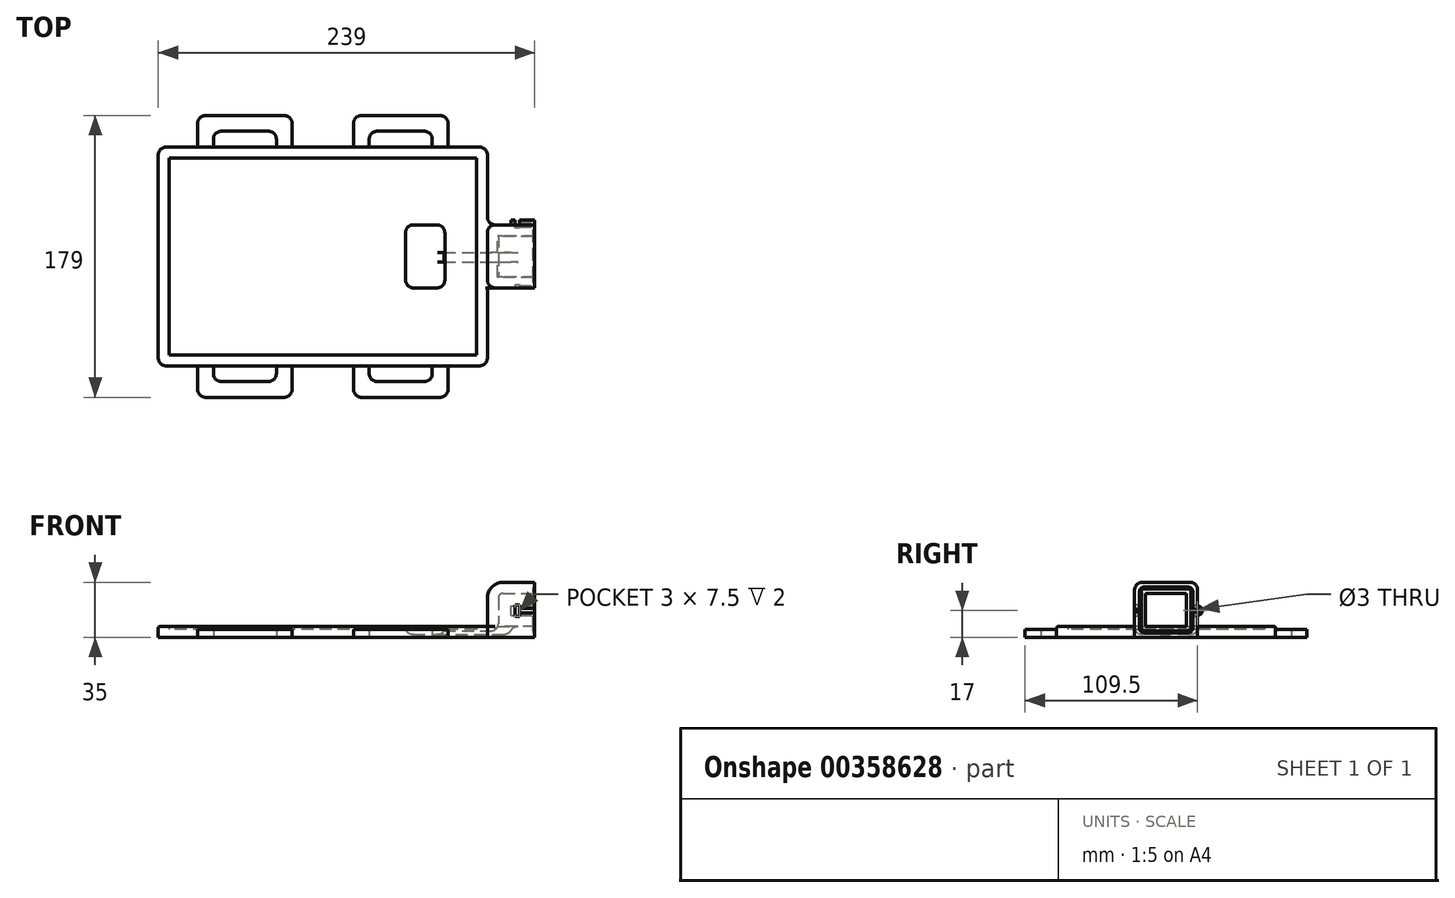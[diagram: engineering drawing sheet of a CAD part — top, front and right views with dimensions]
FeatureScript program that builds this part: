
annotation { "Feature Type Name" : "Feature", "Feature Type Description" : "" }
export const myFeature = defineFeature(function(context is Context, id is Id, definition is map)
    precondition{}
    {
        {
            var Q0;
            Q0=qCreatedBy(makeId("Top.planeOp"),FACE);
            var sketch = newSketch(context, id + "F0", { "sketchPlane" : qUnion([Q0])});
            skLineSegment(sketch, "E0.bottom", {"start": v(0, 0) * mm, "end": v(195, 0) * mm});
            skLineSegment(sketch, "E0.top", {"start": v(0, 125) * mm, "end": v(195, 125) * mm});
            skLineSegment(sketch, "E0.left", {"start": v(0, 0) * mm, "end": v(0, 125) * mm});
            skLineSegment(sketch, "E0.right", {"start": v(195, 0) * mm, "end": v(195, 125) * mm});
            skLineSegment(sketch, "E1.0", {"start": v(-7, 132) * mm, "end": v(202, 132) * mm});
            skLineSegment(sketch, "E1.1", {"start": v(-7, -7) * mm, "end": v(-7, 132) * mm});
            skLineSegment(sketch, "E1.2", {"start": v(-7, -7) * mm, "end": v(202, -7) * mm});
            skLineSegment(sketch, "E1.3", {"start": v(202, -7) * mm, "end": v(202, 132) * mm});
            skSolve(sketch);
        }
        {
            var Q0;
            Q0=makeQuery(id+"F0.imprint","IMPRINT",FACE,{"disambiguationData":[TD([[makeQuery(id+"F0.imprint","IMPRINT",EDGE,{"derivedFrom":sQuery(id+"F0.wireOp",EDGE,"E0.bottom")}),-1.0]])]});
            var Q1;
            Q1=makeQuery(id+"F0.imprint","IMPRINT",FACE,{"disambiguationData":[TD([[makeQuery(id+"F0.imprint","IMPRINT",EDGE,{"derivedFrom":sQuery(id+"F0.wireOp",EDGE,"E0.bottom")}),1.0]])]});
            extrude(context, id + "F1", {"entities" : qUnion([Q0, Q1]), "depth" : 5 * mm});
        }
        {
            var Q0;
            Q0 = qSketchRegion(id + "F0", true);
            extrude(context, id + "F2", {"entities" : qUnion([Q0]), "operationType" : NewBodyOperationType.ADD, "depth" : 7 * mm});
        }
        {
            var Q0;
            Q0=makeQuery(id+"F1.opExtrude","CAP_FACE",FACE,{"disambiguationData":[OSD([sQuery(id+"F0.wireOp",EDGE,"E1.0"),sQuery(id+"F0.wireOp",EDGE,"E1.1"),sQuery(id+"F0.wireOp",EDGE,"E1.2"),sQuery(id+"F0.wireOp",EDGE,"E1.3")])],"isStart":false});
            var sketch = newSketch(context, id + "F3", { "sketchPlane" : qUnion([Q0])});
            skLineSegment(sketch, "E2.bottom", {"start": v(150, 82.5) * mm, "end": v(175, 82.5) * mm});
            skLineSegment(sketch, "E2.top", {"start": v(150, 42.5) * mm, "end": v(175, 42.5) * mm});
            skLineSegment(sketch, "E2.left", {"start": v(150, 82.5) * mm, "end": v(150, 42.5) * mm});
            skLineSegment(sketch, "E2.right", {"start": v(175, 82.5) * mm, "end": v(175, 42.5) * mm});
            skSolve(sketch);
        }
        {
            var Q0;
            Q0=makeQuery(id+"F3.imprint","IMPRINT",FACE,{"disambiguationData":[TD([[makeQuery(id+"F3.imprint","IMPRINT",EDGE,{"derivedFrom":sQuery(id+"F3.wireOp",EDGE,"E2.bottom")}),-1.0]])]});
            extrude(context, id + "F4", {"entities" : qUnion([Q0]), "operationType" : NewBodyOperationType.REMOVE, "oppositeDirection" : true, "depth" : 3 * mm});
        }
        {
            var Q0;
            Q0=makeQuery(id+"F4.boolean.opBoolean","COPY",EDGE,{"derivedFrom":makeQuery(id+"F4.opExtrude","SWEPT_EDGE",EDGE,{"disambiguationData":[OSD([sQuery(id+"F3.wireOp",EDGE,"E2.bottom"),sQuery(id+"F3.wireOp",EDGE,"E2.left")])]})});
            var Q1;
            Q1=makeQuery(id+"F4.boolean.opBoolean","COPY",EDGE,{"derivedFrom":makeQuery(id+"F4.opExtrude","SWEPT_EDGE",EDGE,{"disambiguationData":[OSD([sQuery(id+"F3.wireOp",EDGE,"E2.bottom"),sQuery(id+"F3.wireOp",EDGE,"E2.right")])]})});
            var Q2;
            Q2=makeQuery(id+"F4.boolean.opBoolean","COPY",EDGE,{"derivedFrom":makeQuery(id+"F4.opExtrude","SWEPT_EDGE",EDGE,{"disambiguationData":[OSD([sQuery(id+"F3.wireOp",EDGE,"E2.top"),sQuery(id+"F3.wireOp",EDGE,"E2.right")])]})});
            var Q3;
            Q3=makeQuery(id+"F4.boolean.opBoolean","COPY",EDGE,{"derivedFrom":makeQuery(id+"F4.opExtrude","SWEPT_EDGE",EDGE,{"disambiguationData":[OSD([sQuery(id+"F3.wireOp",EDGE,"E2.top"),sQuery(id+"F3.wireOp",EDGE,"E2.left")])]})});
            fillet(context, id + "F5", {"entities" : qUnion([Q0, Q1, Q2, Q3]), "radius" : 5 * mm, "tangentPropagation" : true, "allowEdgeOverflow" : false});
        }
        {
            var Q0;
            Q0=makeQuery(id+"F4.boolean.opBoolean","COPY",FACE,{"derivedFrom":makeQuery(id+"F4.opExtrude","CAP_FACE",FACE,{"disambiguationData":[OSD([sQuery(id+"F3.wireOp",EDGE,"E2.bottom"),sQuery(id+"F3.wireOp",EDGE,"E2.top"),sQuery(id+"F3.wireOp",EDGE,"E2.left"),sQuery(id+"F3.wireOp",EDGE,"E2.right")])],"isStart":false})});
            fillet(context, id + "F6", {"entities" : qUnion([Q0]), "radius" : 5 * mm, "tangentPropagation" : true, "allowEdgeOverflow" : false});
        }
        {
            var Q0;
            {var subQ0=sQuery(id+"F0.wireOp",EDGE,"E1.3");Q0=makeQuery(id+"F2.boolean.opBoolean","MERGE",FACE,{"derivedFrom":[makeQuery(id+"F1.opExtrude","SWEPT_FACE",FACE,{"disambiguationData":[OSD([subQ0])]}),makeQuery(id+"F2.opExtrude","SWEPT_FACE",FACE,{"disambiguationData":[OSD([subQ0])]})]});}
            var sketch = newSketch(context, id + "F7", { "sketchPlane" : qUnion([Q0])});
            skLineSegment(sketch, "E3.bottom", {"start": v(42.5, 0) * mm, "end": v(82.5, 0) * mm});
            skLineSegment(sketch, "E3.top", {"start": v(42.5, 35) * mm, "end": v(82.5, 35) * mm});
            skLineSegment(sketch, "E3.left", {"start": v(42.5, 0) * mm, "end": v(42.5, 35) * mm});
            skLineSegment(sketch, "E3.right", {"start": v(82.5, 0) * mm, "end": v(82.5, 35) * mm});
            skSolve(sketch);
        }
        {
            var Q0;
            {var subQ0=sQuery(id+"F7.wireOp",EDGE,"E3.top");Q0=makeQuery(id+"F7.imprint","IMPRINT",FACE,{"disambiguationData":[TD([[makeQuery(id+"F7.imprint","IMPRINT",EDGE,{"derivedFrom":subQ0}),-1.0]])]});}
            var Q1;
            {var subQ0=sQuery(id+"F7.wireOp",EDGE,"E3.bottom");Q1=makeQuery(id+"F7.imprint","IMPRINT",FACE,{"disambiguationData":[TD([[makeQuery(id+"F7.imprint","IMPRINT",EDGE,{"derivedFrom":subQ0}),1.0]])]});}
            extrude(context, id + "F8", {"entities" : qUnion([Q0, Q1]), "operationType" : NewBodyOperationType.ADD, "depth" : 30 * mm});
        }
        {
            var Q0;
            Q0=makeQuery(id+"F8.opExtrude","CAP_EDGE",EDGE,{"disambiguationData":[OSD([sQuery(id+"F7.wireOp",EDGE,"E3.top")])],"isStart":true});
            fillet(context, id + "F9", {"entities" : qUnion([Q0]), "radius" : 10 * mm, "tangentPropagation" : true, "allowEdgeOverflow" : false});
        }
        {
            var Q0;
            Q0=makeQuery(id+"F8.opExtrude","SWEPT_EDGE",EDGE,{"disambiguationData":[OSD([sQuery(id+"F7.wireOp",EDGE,"E3.top"),sQuery(id+"F7.wireOp",EDGE,"E3.left")])]});
            var Q1;
            Q1=makeQuery(id+"F8.opExtrude","SWEPT_EDGE",EDGE,{"disambiguationData":[OSD([sQuery(id+"F7.wireOp",EDGE,"E3.top"),sQuery(id+"F7.wireOp",EDGE,"E3.right")])]});
            fillet(context, id + "F10", {"entities" : qUnion([Q0, Q1]), "radius" : 5 * mm, "tangentPropagation" : true, "allowEdgeOverflow" : false});
        }
        {
            var Q0;
            {var subQ0=sQuery(id+"F0.wireOp",EDGE,"E1.3");var subQ1=sQuery(id+"F7.wireOp",EDGE,"E3.left");Q0=makeQuery(id+"F8.boolean.opBoolean","SPLIT",EDGE,{"disambiguationData":[topologyDisambiguationEdgeConnected([makeQuery(id+"F1.opExtrude","SWEPT_FACE",FACE,{"disambiguationData":[OSD([subQ0])]})])],"derivedFrom":makeQuery(id+"F8.opExtrude","CAP_EDGE",EDGE,{"disambiguationData":[OSD([subQ1])],"isStart":true})});}
            var Q1;
            {var subQ0=sQuery(id+"F0.wireOp",EDGE,"E1.3");var subQ1=sQuery(id+"F7.wireOp",EDGE,"E3.right");Q1=makeQuery(id+"F8.boolean.opBoolean","SPLIT",EDGE,{"disambiguationData":[topologyDisambiguationEdgeConnected([makeQuery(id+"F1.opExtrude","SWEPT_FACE",FACE,{"disambiguationData":[OSD([subQ0])]})])],"derivedFrom":makeQuery(id+"F8.opExtrude","CAP_EDGE",EDGE,{"disambiguationData":[OSD([subQ1])],"isStart":true})});}
            fillet(context, id + "F11", {"entities" : qUnion([Q0, Q1]), "radius" : 5 * mm, "tangentPropagation" : true, "allowEdgeOverflow" : false});
        }
        {
            var Q0;
            Q0=makeQuery(id+"F8.opExtrude","CAP_FACE",FACE,{"disambiguationData":[OSD([sQuery(id+"F7.wireOp",EDGE,"E3.bottom"),sQuery(id+"F7.wireOp",EDGE,"E3.top"),sQuery(id+"F7.wireOp",EDGE,"E3.left"),sQuery(id+"F7.wireOp",EDGE,"E3.right")])],"isStart":false});
            shell(context, id + "F12", {"entities" : qUnion([Q0]), "thickness" : 7 * mm});
        }
        {
            var Q0;
            Q0=makeQuery(id+"F8.opExtrude","CAP_FACE",FACE,{"disambiguationData":[OSD([sQuery(id+"F7.wireOp",EDGE,"E3.bottom"),sQuery(id+"F7.wireOp",EDGE,"E3.top"),sQuery(id+"F7.wireOp",EDGE,"E3.left"),sQuery(id+"F7.wireOp",EDGE,"E3.right")])],"isStart":false});
            var sketch = newSketch(context, id + "F13", { "sketchPlane" : qUnion([Q0])});
            skPoint(sketch, "E4.0", {"position": v(43.96, 33.54) * mm});
            skPoint(sketch, "E5.0", {"position": v(81.04, 33.54) * mm});
            skLineSegment(sketch, "E6.0", {"start": v(48.5, 32) * mm, "end": v(76.5, 32) * mm});
            skLineSegment(sketch, "E6.1", {"start": v(45.5, 6) * mm, "end": v(45.5, 29) * mm});
            skLineSegment(sketch, "E6.2", {"start": v(48.5, 3) * mm, "end": v(76.5, 3) * mm});
            skLineSegment(sketch, "E6.3", {"start": v(79.5, 6) * mm, "end": v(79.5, 29) * mm});
            skPoint(sketch, "E7.visualSharp", {"position": v(45.5, 32) * mm});
            skArc(sketch, "E7.filletArc", {"start": v(48.5, 32) * mm, "mid": v(46.38, 31.12) * mm, "end": v(45.5, 29) * mm});
            skPoint(sketch, "E8.visualSharp", {"position": v(79.5, 32) * mm});
            skArc(sketch, "E8.filletArc", {"start": v(79.5, 29) * mm, "mid": v(78.62, 31.12) * mm, "end": v(76.5, 32) * mm});
            skPoint(sketch, "E9.visualSharp", {"position": v(45.5, 3) * mm});
            skArc(sketch, "E9.filletArc", {"start": v(45.5, 6) * mm, "mid": v(46.38, 3.88) * mm, "end": v(48.5, 3) * mm});
            skPoint(sketch, "E10.visualSharp", {"position": v(79.5, 3) * mm});
            skArc(sketch, "E10.filletArc", {"start": v(76.5, 3) * mm, "mid": v(78.62, 3.88) * mm, "end": v(79.5, 6) * mm});
            skLineSegment(sketch, "E11.0", {"start": v(48.7, 30.8) * mm, "end": v(76.3, 30.8) * mm});
            skLineSegment(sketch, "E11.1", {"start": v(46.7, 6.2) * mm, "end": v(46.7, 28.8) * mm});
            skLineSegment(sketch, "E11.2", {"start": v(48.7, 4.2) * mm, "end": v(76.3, 4.2) * mm});
            skLineSegment(sketch, "E11.3", {"start": v(78.3, 6.2) * mm, "end": v(78.3, 28.8) * mm});
            skPoint(sketch, "E12.visualSharp", {"position": v(46.7, 30.8) * mm});
            skArc(sketch, "E12.filletArc", {"start": v(48.7, 30.8) * mm, "mid": v(47.29, 30.21) * mm, "end": v(46.7, 28.8) * mm});
            skPoint(sketch, "E13.visualSharp", {"position": v(78.3, 30.8) * mm});
            skArc(sketch, "E13.filletArc", {"start": v(78.3, 28.8) * mm, "mid": v(77.71, 30.21) * mm, "end": v(76.3, 30.8) * mm});
            skPoint(sketch, "E14.visualSharp", {"position": v(78.3, 4.2) * mm});
            skArc(sketch, "E14.filletArc", {"start": v(76.3, 4.2) * mm, "mid": v(77.71, 4.79) * mm, "end": v(78.3, 6.2) * mm});
            skPoint(sketch, "E15.visualSharp", {"position": v(46.7, 4.2) * mm});
            skArc(sketch, "E15.filletArc", {"start": v(46.7, 6.2) * mm, "mid": v(47.29, 4.79) * mm, "end": v(48.7, 4.2) * mm});
            skPoint(sketch, "E16.0.end.orphan", {"position": v(42.5, 30) * mm});
            skPoint(sketch, "E16.0.start.orphan", {"position": v(42.5, 0) * mm});
            skPoint(sketch, "E17.0.start.orphan", {"position": v(47.5, 35) * mm});
            skPoint(sketch, "E18.0.end.orphan", {"position": v(77.5, 35) * mm});
            skPoint(sketch, "E19.0.end.orphan", {"position": v(82.5, 30) * mm});
            skPoint(sketch, "E19.0.start.orphan", {"position": v(82.5, 0) * mm});
            skSolve(sketch);
        }
        {
            var Q0;
            Q0=makeQuery(id+"F13.imprint","IMPRINT",FACE,{"disambiguationData":[TD([[makeQuery(id+"F13.imprint","IMPRINT",EDGE,{"derivedFrom":sQuery(id+"F13.wireOp",EDGE,"E6.0")}),-1.0]])]});
            extrude(context, id + "F14", {"entities" : qUnion([Q0]), "operationType" : NewBodyOperationType.REMOVE, "oppositeDirection" : true, "depth" : 1 * mm});
        }
        {
            var Q0;
            {var subQ0=sQuery(id+"F7.wireOp",EDGE,"E3.right");var subQ1=sQuery(id+"F7.wireOp",EDGE,"E3.left");var subQ2=sQuery(id+"F7.wireOp",EDGE,"E3.top");var subQ3=sQuery(id+"F7.wireOp",EDGE,"E3.bottom");Q0=makeQuery(id+"F14.boolean.opBoolean","SPLIT",FACE,{"disambiguationData":[TD([makeQuery(id+"F8.opExtrude","SWEPT_FACE",FACE,{"disambiguationData":[OSD([subQ3])]})])],"derivedFrom":makeQuery(id+"F8.opExtrude","CAP_FACE",FACE,{"disambiguationData":[OSD([subQ3,subQ2,subQ1,subQ0])],"isStart":false})});}
            var sketch = newSketch(context, id + "F15", { "sketchPlane" : qUnion([Q0])});
            skCircle(sketch, "E20", {"center": v(42.5, 17) * mm, "radius": 3 * mm});
            skCircle(sketch, "E21", {"center": v(42.5, 17) * mm, "radius": 1.5 * mm});
            skCircle(sketch, "E22", {"center": v(82.5, 17) * mm, "radius": 1.5 * mm});
            skCircle(sketch, "E23", {"center": v(82.5, 17) * mm, "radius": 3 * mm});
            skSolve(sketch);
        }
        {
            var Q0;
            {var subQ0=sQuery(id+"F15.wireOp",EDGE,"E20");var subQ1=makeQuery(id+"F8.opExtrude","CAP_EDGE",EDGE,{"disambiguationData":[OSD([sQuery(id+"F7.wireOp",EDGE,"E3.left")])],"isStart":false});var subQ2=makeQuery(id+"F15.imprint","INTERSECT",VERTEX,{"disambiguationData":[OD(0.0)],"derivedFrom":[subQ1,subQ0]});Q0=makeQuery(id+"F15.imprint","IMPRINT",FACE,{"disambiguationData":[TD([[makeQuery(id+"F15.imprint","IMPRINT",EDGE,{"disambiguationData":[TD([[subQ2,-1.0]])],"derivedFrom":subQ0}),1.0]])]});}
            var Q1;
            {var subQ0=sQuery(id+"F15.wireOp",EDGE,"E22");var subQ1=makeQuery(id+"F8.opExtrude","CAP_EDGE",EDGE,{"disambiguationData":[OSD([sQuery(id+"F7.wireOp",EDGE,"E3.right")])],"isStart":false});var subQ2=makeQuery(id+"F15.imprint","INTERSECT",VERTEX,{"disambiguationData":[OD(0.0)],"derivedFrom":[subQ1,subQ0]});Q1=makeQuery(id+"F15.imprint","IMPRINT",FACE,{"disambiguationData":[TD([[makeQuery(id+"F15.imprint","IMPRINT",EDGE,{"disambiguationData":[TD([[subQ2,1.0]])],"derivedFrom":subQ0}),-1.0]])]});}
            var Q2;
            {var subQ0=sQuery(id+"F15.wireOp",EDGE,"E22");var subQ1=makeQuery(id+"F8.opExtrude","CAP_EDGE",EDGE,{"disambiguationData":[OSD([sQuery(id+"F7.wireOp",EDGE,"E3.right")])],"isStart":false});var subQ2=makeQuery(id+"F15.imprint","INTERSECT",VERTEX,{"disambiguationData":[OD(0.0)],"derivedFrom":[subQ1,subQ0]});Q2=makeQuery(id+"F15.imprint","IMPRINT",FACE,{"disambiguationData":[TD([[makeQuery(id+"F15.imprint","IMPRINT",EDGE,{"disambiguationData":[TD([[subQ2,1.0]])],"derivedFrom":subQ0}),1.0]])]});}
            var Q3;
            {var subQ0=sQuery(id+"F15.wireOp",EDGE,"E21");var subQ1=makeQuery(id+"F8.opExtrude","CAP_EDGE",EDGE,{"disambiguationData":[OSD([sQuery(id+"F7.wireOp",EDGE,"E3.left")])],"isStart":false});var subQ2=makeQuery(id+"F15.imprint","INTERSECT",VERTEX,{"disambiguationData":[OD(0.0)],"derivedFrom":[subQ1,subQ0]});Q3=makeQuery(id+"F15.imprint","IMPRINT",FACE,{"disambiguationData":[TD([[makeQuery(id+"F15.imprint","IMPRINT",EDGE,{"disambiguationData":[TD([[subQ2,-1.0]])],"derivedFrom":subQ0}),1.0]])]});}
            extrude(context, id + "F16", {"entities" : qUnion([Q0, Q1, Q2, Q3]), "operationType" : NewBodyOperationType.ADD, "oppositeDirection" : true, "depth" : 15 * mm});
        }
        {
            var Q0;
            {var subQ0=sQuery(id+"F15.wireOp",EDGE,"E22");var subQ1=makeQuery(id+"F8.opExtrude","CAP_EDGE",EDGE,{"disambiguationData":[OSD([sQuery(id+"F7.wireOp",EDGE,"E3.right")])],"isStart":false});var subQ2=makeQuery(id+"F15.imprint","INTERSECT",VERTEX,{"disambiguationData":[OD(0.0)],"derivedFrom":[subQ1,subQ0]});Q0=makeQuery(id+"F15.imprint","IMPRINT",FACE,{"disambiguationData":[TD([[makeQuery(id+"F15.imprint","IMPRINT",EDGE,{"disambiguationData":[TD([[subQ2,1.0]])],"derivedFrom":subQ0}),1.0]])]});}
            var Q1;
            {var subQ0=sQuery(id+"F15.wireOp",EDGE,"E22");var subQ1=makeQuery(id+"F8.opExtrude","CAP_EDGE",EDGE,{"disambiguationData":[OSD([sQuery(id+"F7.wireOp",EDGE,"E3.right")])],"isStart":false});var subQ2=makeQuery(id+"F15.imprint","INTERSECT",VERTEX,{"disambiguationData":[OD(0.0)],"derivedFrom":[subQ1,subQ0]});Q1=makeQuery(id+"F15.imprint","IMPRINT",FACE,{"disambiguationData":[TD([[makeQuery(id+"F15.imprint","IMPRINT",EDGE,{"disambiguationData":[TD([[subQ2,-1.0]])],"derivedFrom":subQ0}),1.0]])]});}
            var Q2;
            {var subQ0=sQuery(id+"F15.wireOp",EDGE,"E21");var subQ1=makeQuery(id+"F8.opExtrude","CAP_EDGE",EDGE,{"disambiguationData":[OSD([sQuery(id+"F7.wireOp",EDGE,"E3.left")])],"isStart":false});var subQ2=makeQuery(id+"F15.imprint","INTERSECT",VERTEX,{"disambiguationData":[OD(0.0)],"derivedFrom":[subQ1,subQ0]});Q2=makeQuery(id+"F15.imprint","IMPRINT",FACE,{"disambiguationData":[TD([[makeQuery(id+"F15.imprint","IMPRINT",EDGE,{"disambiguationData":[TD([[subQ2,-1.0]])],"derivedFrom":subQ0}),1.0]])]});}
            var Q3;
            {var subQ0=sQuery(id+"F15.wireOp",EDGE,"E21");var subQ1=makeQuery(id+"F8.opExtrude","CAP_EDGE",EDGE,{"disambiguationData":[OSD([sQuery(id+"F7.wireOp",EDGE,"E3.left")])],"isStart":false});var subQ2=makeQuery(id+"F15.imprint","INTERSECT",VERTEX,{"disambiguationData":[OD(0.0)],"derivedFrom":[subQ1,subQ0]});Q3=makeQuery(id+"F15.imprint","IMPRINT",FACE,{"disambiguationData":[TD([[makeQuery(id+"F15.imprint","IMPRINT",EDGE,{"disambiguationData":[TD([[subQ2,1.0]])],"derivedFrom":subQ0}),1.0]])]});}
            extrude(context, id + "F17", {"entities" : qUnion([Q0, Q1, Q2, Q3]), "operationType" : NewBodyOperationType.REMOVE, "oppositeDirection" : true, "depth" : 10 * mm});
        }
        {
            var Q0;
            Q0=makeQuery(id+"F8.opExtrude","SWEPT_FACE",FACE,{"disambiguationData":[OSD([sQuery(id+"F7.wireOp",EDGE,"E3.left")])]});
            var sketch = newSketch(context, id + "F18", { "sketchPlane" : qUnion([Q0])});
            skLineSegment(sketch, "E24.bottom", {"start": v(219.5, 20.7) * mm, "end": v(222.5, 20.7) * mm});
            skLineSegment(sketch, "E24.top", {"start": v(219.5, 13.2) * mm, "end": v(222.5, 13.2) * mm});
            skLineSegment(sketch, "E24.left", {"start": v(219.5, 20.7) * mm, "end": v(219.5, 13.2) * mm});
            skLineSegment(sketch, "E24.right", {"start": v(222.5, 20.7) * mm, "end": v(222.5, 13.2) * mm});
            skSolve(sketch);
        }
        {
            var Q0;
            Q0 = qSketchRegion(id + "F18", true);
            extrude(context, id + "F19", {"entities" : qUnion([Q0]), "operationType" : NewBodyOperationType.REMOVE, "oppositeDirection" : true, "depth" : 2 * mm, "hasSecondDirection" : true, "secondDirectionOppositeDirection" : false, "secondDirectionDepth" : 25 * mm});
        }
        {
            var Q0;
            Q0=makeQuery(id+"F8.opExtrude","SWEPT_FACE",FACE,{"disambiguationData":[OSD([sQuery(id+"F7.wireOp",EDGE,"E3.right")])]});
            var sketch = newSketch(context, id + "F20", { "sketchPlane" : qUnion([Q0])});
            skLineSegment(sketch, "E25.bottom", {"start": v(-222.5, 20.7) * mm, "end": v(-219.5, 20.7) * mm});
            skLineSegment(sketch, "E25.top", {"start": v(-222.5, 13.2) * mm, "end": v(-219.5, 13.2) * mm});
            skLineSegment(sketch, "E25.left", {"start": v(-222.5, 20.7) * mm, "end": v(-222.5, 13.2) * mm});
            skLineSegment(sketch, "E25.right", {"start": v(-219.5, 20.7) * mm, "end": v(-219.5, 13.2) * mm});
            skSolve(sketch);
        }
        {
            var Q0;
            Q0 = qSketchRegion(id + "F20", true);
            extrude(context, id + "F21", {"entities" : qUnion([Q0]), "operationType" : NewBodyOperationType.REMOVE, "oppositeDirection" : true, "depth" : 2 * mm, "hasSecondDirection" : true, "secondDirectionOppositeDirection" : false, "secondDirectionDepth" : 25 * mm});
        }
        {
            var Q0;
            {var subQ0=sQuery(id+"F0.wireOp",EDGE,"E1.3");var subQ1=sQuery(id+"F0.wireOp",EDGE,"E1.0");Q0=makeQuery(id+"F2.boolean.opBoolean","MERGE",EDGE,{"derivedFrom":[makeQuery(id+"F1.opExtrude","SWEPT_EDGE",EDGE,{"disambiguationData":[OSD([subQ1,subQ0])]}),makeQuery(id+"F2.opExtrude","SWEPT_EDGE",EDGE,{"disambiguationData":[OSD([subQ1,subQ0])]})]});}
            var Q1;
            {var subQ0=sQuery(id+"F0.wireOp",EDGE,"E1.3");var subQ1=sQuery(id+"F0.wireOp",EDGE,"E1.2");Q1=makeQuery(id+"F2.boolean.opBoolean","MERGE",EDGE,{"derivedFrom":[makeQuery(id+"F1.opExtrude","SWEPT_EDGE",EDGE,{"disambiguationData":[OSD([subQ1,subQ0])]}),makeQuery(id+"F2.opExtrude","SWEPT_EDGE",EDGE,{"disambiguationData":[OSD([subQ1,subQ0])]})]});}
            var Q2;
            {var subQ0=sQuery(id+"F0.wireOp",EDGE,"E1.1");var subQ1=sQuery(id+"F0.wireOp",EDGE,"E1.0");Q2=makeQuery(id+"F2.boolean.opBoolean","MERGE",EDGE,{"derivedFrom":[makeQuery(id+"F1.opExtrude","SWEPT_EDGE",EDGE,{"disambiguationData":[OSD([subQ1,subQ0])]}),makeQuery(id+"F2.opExtrude","SWEPT_EDGE",EDGE,{"disambiguationData":[OSD([subQ1,subQ0])]})]});}
            var Q3;
            {var subQ0=sQuery(id+"F0.wireOp",EDGE,"E1.2");var subQ1=sQuery(id+"F0.wireOp",EDGE,"E1.1");Q3=makeQuery(id+"F2.boolean.opBoolean","MERGE",EDGE,{"derivedFrom":[makeQuery(id+"F1.opExtrude","SWEPT_EDGE",EDGE,{"disambiguationData":[OSD([subQ1,subQ0])]}),makeQuery(id+"F2.opExtrude","SWEPT_EDGE",EDGE,{"disambiguationData":[OSD([subQ1,subQ0])]})]});}
            fillet(context, id + "F22", {"entities" : qUnion([Q0, Q1, Q2, Q3]), "radius" : 5 * mm, "tangentPropagation" : true, "allowEdgeOverflow" : false});
        }
        {
            var Q0;
            {var subQ0=sQuery(id+"F0.wireOp",EDGE,"E1.3");var subQ1=sQuery(id+"F0.wireOp",EDGE,"E1.2");Q0=makeQuery(id+"F22.opFillet","BLEND_EDGE",EDGE,{"blendedFrom":[makeQuery(id+"F2.boolean.opBoolean","MERGE",EDGE,{"derivedFrom":[makeQuery(id+"F1.opExtrude","SWEPT_EDGE",EDGE,{"disambiguationData":[OSD([subQ1,subQ0])]}),makeQuery(id+"F2.opExtrude","SWEPT_EDGE",EDGE,{"disambiguationData":[OSD([subQ1,subQ0])]})]}),makeQuery(id+"F2.opExtrude","CAP_FACE",FACE,{"disambiguationData":[OSD([sQuery(id+"F0.wireOp",EDGE,"E0.bottom"),sQuery(id+"F0.wireOp",EDGE,"E0.top"),sQuery(id+"F0.wireOp",EDGE,"E0.left"),sQuery(id+"F0.wireOp",EDGE,"E0.right"),sQuery(id+"F0.wireOp",EDGE,"E1.0"),sQuery(id+"F0.wireOp",EDGE,"E1.1"),subQ1,subQ0])],"isStart":false})],"blendedInto":[makeQuery(id+"F2.opExtrude","CAP_FACE",FACE,{"disambiguationData":[OSD([sQuery(id+"F0.wireOp",EDGE,"E0.bottom"),sQuery(id+"F0.wireOp",EDGE,"E0.top"),sQuery(id+"F0.wireOp",EDGE,"E0.left"),sQuery(id+"F0.wireOp",EDGE,"E0.right"),sQuery(id+"F0.wireOp",EDGE,"E1.0"),sQuery(id+"F0.wireOp",EDGE,"E1.1"),subQ1,subQ0])],"isStart":false})]});}
            fillet(context, id + "F23", {"entities" : qUnion([Q0]), "radius" : 1 * mm, "tangentPropagation" : true, "allowEdgeOverflow" : false});
        }
        {
            var Q0;
            Q0=makeQuery(id+"F4.boolean.opBoolean","COPY",FACE,{"derivedFrom":makeQuery(id+"F4.opExtrude","CAP_FACE",FACE,{"disambiguationData":[OSD([sQuery(id+"F3.wireOp",EDGE,"E2.bottom"),sQuery(id+"F3.wireOp",EDGE,"E2.top"),sQuery(id+"F3.wireOp",EDGE,"E2.left"),sQuery(id+"F3.wireOp",EDGE,"E2.right")])],"isStart":false})});
            var sketch = newSketch(context, id + "F24", { "sketchPlane" : qUnion([Q0])});
            skLineSegment(sketch, "E26", {"start": v(170.42, 62.5) * mm, "end": v(217.7, 62.5) * mm});
            skSolve(sketch);
        }
        {
            var Q0;
            {var subQ0=sQuery(id+"F3.wireOp",EDGE,"E2.right");Q0=makeQuery(id+"F6.opFillet","BLEND_EDGE",EDGE,{"blendedFrom":[makeQuery(id+"F4.boolean.opBoolean","COPY",EDGE,{"derivedFrom":makeQuery(id+"F4.opExtrude","CAP_EDGE",EDGE,{"disambiguationData":[OSD([subQ0])],"isStart":false})}),makeQuery(id+"F4.boolean.opBoolean","COPY",FACE,{"derivedFrom":makeQuery(id+"F4.opExtrude","CAP_FACE",FACE,{"disambiguationData":[OSD([sQuery(id+"F3.wireOp",EDGE,"E2.bottom"),sQuery(id+"F3.wireOp",EDGE,"E2.top"),sQuery(id+"F3.wireOp",EDGE,"E2.left"),subQ0])],"isStart":false})})],"blendedInto":[makeQuery(id+"F4.boolean.opBoolean","COPY",FACE,{"derivedFrom":makeQuery(id+"F4.opExtrude","CAP_FACE",FACE,{"disambiguationData":[OSD([sQuery(id+"F3.wireOp",EDGE,"E2.bottom"),sQuery(id+"F3.wireOp",EDGE,"E2.top"),sQuery(id+"F3.wireOp",EDGE,"E2.left"),subQ0])],"isStart":false})})]});}
            cPoint(context, id + "F25", {"entities" : qUnion([Q0]), "parameter" : 0.5});
        }
        {
            var Q0;
            Q0=sQuery(id+"F24.wireOp",EDGE,"E26");
            var Q1;
            Q1 = qCreatedBy(id + "F25" ,VERTEX);
            cPlane(context, id + "F26", {"entities" : qUnion([Q0, Q1]), "cplaneType" : CPlaneType.CURVE_POINT, "offset" : 25 * mm, "width" : 150 * mm, "height" : 150 * mm});
        }
        {
            var Q0;
            Q0=qCreatedBy(id+"F26.planeOp",FACE);
            var sketch = newSketch(context, id + "F27", { "sketchPlane" : qUnion([Q0])});
            skLineSegment(sketch, "E27.bottom", {"start": v(64.88, 2) * mm, "end": v(58.88, 2) * mm});
            skLineSegment(sketch, "E27.top", {"start": v(64.88, 4) * mm, "end": v(58.88, 4) * mm});
            skLineSegment(sketch, "E27.left", {"start": v(64.88, 2) * mm, "end": v(64.88, 4) * mm});
            skLineSegment(sketch, "E27.right", {"start": v(58.88, 2) * mm, "end": v(58.88, 4) * mm});
            skSolve(sketch);
        }
        {
            var Q0;
            Q0=makeQuery(id+"F27.imprint","IMPRINT",FACE,{"disambiguationData":[TD([[makeQuery(id+"F27.imprint","IMPRINT",EDGE,{"derivedFrom":sQuery(id+"F27.wireOp",EDGE,"E27.bottom")}),-1.0]])]});
            var Q1;
            Q1 = qConstructionFilter(qBodyType(qCreatedBy(id + "F24" ,EDGE), BodyType.WIRE), ConstructionObject.NO);
            sweep(context, id + "F28", {"operationType" : NewBodyOperationType.REMOVE, "profiles" : qUnion([Q0]), "path" : qUnion([Q1])});
        }
        {
            var Q0;
            Q0=makeQuery(id+"F12.opShell","OFFSET_FACE",FACE,{"disambiguationData":[OSD([sQuery(id+"F0.wireOp",EDGE,"E1.0"),sQuery(id+"F0.wireOp",EDGE,"E1.1"),sQuery(id+"F0.wireOp",EDGE,"E1.2"),sQuery(id+"F0.wireOp",EDGE,"E1.3"),sQuery(id+"F7.wireOp",EDGE,"E3.bottom")])]});
            var sketch = newSketch(context, id + "F29", { "sketchPlane" : qUnion([Q0])});
            skLineSegment(sketch, "E28.bottom", {"start": v(209, 58.88) * mm, "end": v(217.7, 58.88) * mm});
            skLineSegment(sketch, "E28.top", {"start": v(209, 64.88) * mm, "end": v(217.7, 64.88) * mm});
            skLineSegment(sketch, "E28.left", {"start": v(209, 58.88) * mm, "end": v(209, 64.88) * mm});
            skLineSegment(sketch, "E28.right", {"start": v(217.7, 58.88) * mm, "end": v(217.7, 64.88) * mm});
            skSolve(sketch);
        }
        {
            var Q0;
            Q0 = qSketchRegion(id + "F29", true);
            extrude(context, id + "F30", {"entities" : qUnion([Q0]), "operationType" : NewBodyOperationType.REMOVE, "oppositeDirection" : true, "depth" : 5 * mm});
        }
        {
            var Q0;
            Q0=makeQuery(id+"F30.boolean.opBoolean","INTERSECT",EDGE,{"derivedFrom":[makeQuery(id+"F28.boolean.opBoolean","COPY",FACE,{"derivedFrom":makeQuery(id+"F28.opSweep","SWEPT_FACE",FACE,{"disambiguationData":[OSD([sQuery(id+"F24.wireOp",EDGE,"E26"),sQuery(id+"F27.wireOp",EDGE,"E27.top")])]})}),makeQuery(id+"F30.opExtrude","SWEPT_FACE",FACE,{"disambiguationData":[OSD([sQuery(id+"F29.wireOp",EDGE,"E28.left")])]})]});
            fillet(context, id + "F31", {"entities" : qUnion([Q0]), "radius" : 5 * mm, "tangentPropagation" : true, "allowEdgeOverflow" : false});
        }
        {
            var Q0;
            Q0=makeQuery(id+"F8.boolean.opBoolean","MERGE",FACE,{"derivedFrom":[makeQuery(id+"F1.opExtrude","CAP_FACE",FACE,{"disambiguationData":[OSD([sQuery(id+"F0.wireOp",EDGE,"E1.0"),sQuery(id+"F0.wireOp",EDGE,"E1.1"),sQuery(id+"F0.wireOp",EDGE,"E1.2"),sQuery(id+"F0.wireOp",EDGE,"E1.3")])],"isStart":true}),makeQuery(id+"F8.opExtrude","SWEPT_FACE",FACE,{"disambiguationData":[OSD([sQuery(id+"F7.wireOp",EDGE,"E3.bottom")])]})]});
            var sketch = newSketch(context, id + "F32", { "sketchPlane" : qUnion([Q0])});
            skLineSegment(sketch, "E29.bottom", {"start": v(18, 7) * mm, "end": v(28, 7) * mm});
            skLineSegment(sketch, "E29.top", {"start": v(18, 27) * mm, "end": v(78, 27) * mm});
            skLineSegment(sketch, "E29.left", {"start": v(18, 7) * mm, "end": v(18, 27) * mm});
            skLineSegment(sketch, "E29.right", {"start": v(78, 7) * mm, "end": v(78, 27) * mm});
            skLineSegment(sketch, "E30.bottom", {"start": v(117, 7) * mm, "end": v(127, 7) * mm});
            skLineSegment(sketch, "E30.top", {"start": v(117, 27) * mm, "end": v(177, 27) * mm});
            skLineSegment(sketch, "E30.left", {"start": v(117, 7) * mm, "end": v(117, 27) * mm});
            skLineSegment(sketch, "E30.right", {"start": v(177, 7) * mm, "end": v(177, 27) * mm});
            skLineSegment(sketch, "E31.top", {"start": v(28, 17) * mm, "end": v(68, 17) * mm});
            skLineSegment(sketch, "E31.left", {"start": v(28, 7) * mm, "end": v(28, 17) * mm});
            skLineSegment(sketch, "E31.right", {"start": v(68, 7) * mm, "end": v(68, 17) * mm});
            skLineSegment(sketch, "E32.top", {"start": v(127, 17) * mm, "end": v(167, 17) * mm});
            skLineSegment(sketch, "E32.left", {"start": v(127, 7) * mm, "end": v(127, 17) * mm});
            skLineSegment(sketch, "E32.right", {"start": v(167, 7) * mm, "end": v(167, 17) * mm});
            skLineSegment(sketch, "E33.top", {"start": v(18, -152) * mm, "end": v(78, -152) * mm});
            skLineSegment(sketch, "E33.left", {"start": v(18, -132) * mm, "end": v(18, -152) * mm});
            skLineSegment(sketch, "E33.right", {"start": v(78, -132) * mm, "end": v(78, -152) * mm});
            skPoint(sketch, "E34.oppositeSnap0", {"position": v(18, -142) * mm});
            skLineSegment(sketch, "E34.top", {"start": v(28, -142) * mm, "end": v(68, -142) * mm});
            skLineSegment(sketch, "E34.left", {"start": v(28, -132) * mm, "end": v(28, -142) * mm});
            skLineSegment(sketch, "E34.right", {"start": v(68, -132) * mm, "end": v(68, -142) * mm});
            skLineSegment(sketch, "E35.top", {"start": v(117, -152) * mm, "end": v(177, -152) * mm});
            skLineSegment(sketch, "E35.left", {"start": v(117, -132) * mm, "end": v(117, -152) * mm});
            skLineSegment(sketch, "E35.right", {"start": v(177, -132) * mm, "end": v(177, -152) * mm});
            skLineSegment(sketch, "E36.top", {"start": v(127, -142) * mm, "end": v(167, -142) * mm});
            skLineSegment(sketch, "E36.left", {"start": v(127, -132) * mm, "end": v(127, -142) * mm});
            skLineSegment(sketch, "E36.right", {"start": v(167, -132) * mm, "end": v(167, -142) * mm});
            skLineSegment(sketch, "E37.trimOffspring", {"start": v(68, -132) * mm, "end": v(78, -132) * mm});
            skLineSegment(sketch, "E38.trimOffspring", {"start": v(167, -132) * mm, "end": v(177, -132) * mm});
            skLineSegment(sketch, "E39.trimOffspring", {"start": v(68, 7) * mm, "end": v(78, 7) * mm});
            skLineSegment(sketch, "E40.trimOffspring", {"start": v(167, 7) * mm, "end": v(177, 7) * mm});
            skSolve(sketch);
        }
        {
            var Q0;
            Q0=makeQuery(id+"F32.imprint","IMPRINT",FACE,{"disambiguationData":[TD([[makeQuery(id+"F32.imprint","IMPRINT",EDGE,{"derivedFrom":sQuery(id+"F32.wireOp",EDGE,"E29.bottom")}),1.0]])]});
            var Q1;
            Q1=makeQuery(id+"F32.imprint","IMPRINT",FACE,{"disambiguationData":[TD([[makeQuery(id+"F32.imprint","IMPRINT",EDGE,{"derivedFrom":sQuery(id+"F32.wireOp",EDGE,"E30.bottom")}),1.0]])]});
            var Q2;
            Q2=makeQuery(id+"F32.imprint","IMPRINT",FACE,{"disambiguationData":[TD([[makeQuery(id+"F32.imprint","IMPRINT",EDGE,{"derivedFrom":sQuery(id+"F32.wireOp",EDGE,"E35.top")}),1.0]])]});
            var Q3;
            Q3=makeQuery(id+"F32.imprint","IMPRINT",FACE,{"disambiguationData":[TD([[makeQuery(id+"F32.imprint","IMPRINT",EDGE,{"derivedFrom":sQuery(id+"F32.wireOp",EDGE,"E33.top")}),1.0]])]});
            extrude(context, id + "F33", {"entities" : qUnion([Q0, Q1, Q2, Q3]), "operationType" : NewBodyOperationType.ADD, "oppositeDirection" : true, "depth" : 5 * mm});
        }
        {
            var Q0;
            Q0=makeQuery(id+"F33.opExtrude","SWEPT_EDGE",EDGE,{"disambiguationData":[OSD([sQuery(id+"F32.wireOp",EDGE,"E29.top"),sQuery(id+"F32.wireOp",EDGE,"E29.left")])]});
            var Q1;
            Q1=makeQuery(id+"F33.opExtrude","SWEPT_EDGE",EDGE,{"disambiguationData":[OSD([sQuery(id+"F32.wireOp",EDGE,"E33.top"),sQuery(id+"F32.wireOp",EDGE,"E33.left")])]});
            var Q2;
            Q2=makeQuery(id+"F33.opExtrude","SWEPT_EDGE",EDGE,{"disambiguationData":[OSD([sQuery(id+"F32.wireOp",EDGE,"E33.top"),sQuery(id+"F32.wireOp",EDGE,"E33.right")])]});
            var Q3;
            Q3=makeQuery(id+"F33.opExtrude","SWEPT_EDGE",EDGE,{"disambiguationData":[OSD([sQuery(id+"F32.wireOp",EDGE,"E35.top"),sQuery(id+"F32.wireOp",EDGE,"E35.left")])]});
            var Q4;
            Q4=makeQuery(id+"F33.opExtrude","SWEPT_EDGE",EDGE,{"disambiguationData":[OSD([sQuery(id+"F32.wireOp",EDGE,"E35.top"),sQuery(id+"F32.wireOp",EDGE,"E35.right")])]});
            var Q5;
            Q5=makeQuery(id+"F33.opExtrude","SWEPT_EDGE",EDGE,{"disambiguationData":[OSD([sQuery(id+"F32.wireOp",EDGE,"E34.top"),sQuery(id+"F32.wireOp",EDGE,"E34.right")])]});
            var Q6;
            Q6=makeQuery(id+"F33.opExtrude","SWEPT_EDGE",EDGE,{"disambiguationData":[OSD([sQuery(id+"F32.wireOp",EDGE,"E34.top"),sQuery(id+"F32.wireOp",EDGE,"E34.left")])]});
            var Q7;
            Q7=makeQuery(id+"F33.opExtrude","SWEPT_EDGE",EDGE,{"disambiguationData":[OSD([sQuery(id+"F32.wireOp",EDGE,"E36.top"),sQuery(id+"F32.wireOp",EDGE,"E36.right")])]});
            var Q8;
            Q8=makeQuery(id+"F33.opExtrude","SWEPT_EDGE",EDGE,{"disambiguationData":[OSD([sQuery(id+"F32.wireOp",EDGE,"E36.top"),sQuery(id+"F32.wireOp",EDGE,"E36.left")])]});
            var Q9;
            Q9=makeQuery(id+"F33.opExtrude","SWEPT_EDGE",EDGE,{"disambiguationData":[OSD([sQuery(id+"F32.wireOp",EDGE,"E32.top"),sQuery(id+"F32.wireOp",EDGE,"E32.right")])]});
            var Q10;
            Q10=makeQuery(id+"F33.opExtrude","SWEPT_EDGE",EDGE,{"disambiguationData":[OSD([sQuery(id+"F32.wireOp",EDGE,"E32.top"),sQuery(id+"F32.wireOp",EDGE,"E32.left")])]});
            var Q11;
            Q11=makeQuery(id+"F33.opExtrude","SWEPT_EDGE",EDGE,{"disambiguationData":[OSD([sQuery(id+"F32.wireOp",EDGE,"E30.top"),sQuery(id+"F32.wireOp",EDGE,"E30.right")])]});
            var Q12;
            Q12=makeQuery(id+"F33.opExtrude","SWEPT_EDGE",EDGE,{"disambiguationData":[OSD([sQuery(id+"F32.wireOp",EDGE,"E30.top"),sQuery(id+"F32.wireOp",EDGE,"E30.left")])]});
            var Q13;
            Q13=makeQuery(id+"F33.opExtrude","SWEPT_EDGE",EDGE,{"disambiguationData":[OSD([sQuery(id+"F32.wireOp",EDGE,"E29.top"),sQuery(id+"F32.wireOp",EDGE,"E29.right")])]});
            var Q14;
            Q14=makeQuery(id+"F33.opExtrude","SWEPT_EDGE",EDGE,{"disambiguationData":[OSD([sQuery(id+"F0.wireOp",EDGE,"E1.2"),sQuery(id+"F32.wireOp",EDGE,"E29.right"),sQuery(id+"F32.wireOp",EDGE,"E39.trimOffspring")])]});
            var Q15;
            Q15=makeQuery(id+"F33.opExtrude","SWEPT_EDGE",EDGE,{"disambiguationData":[OSD([sQuery(id+"F0.wireOp",EDGE,"E1.2"),sQuery(id+"F32.wireOp",EDGE,"E29.bottom"),sQuery(id+"F32.wireOp",EDGE,"E29.left")])]});
            var Q16;
            Q16=makeQuery(id+"F33.opExtrude","SWEPT_EDGE",EDGE,{"disambiguationData":[OSD([sQuery(id+"F32.wireOp",EDGE,"E31.top"),sQuery(id+"F32.wireOp",EDGE,"E31.right")])]});
            var Q17;
            Q17=makeQuery(id+"F33.opExtrude","SWEPT_EDGE",EDGE,{"disambiguationData":[OSD([sQuery(id+"F32.wireOp",EDGE,"E31.top"),sQuery(id+"F32.wireOp",EDGE,"E31.left")])]});
            var Q18;
            Q18=makeQuery(id+"F33.opExtrude","SWEPT_EDGE",EDGE,{"disambiguationData":[OSD([sQuery(id+"F0.wireOp",EDGE,"E1.0"),sQuery(id+"F32.wireOp",EDGE,"E33.right"),sQuery(id+"F32.wireOp",EDGE,"E37.trimOffspring")])]});
            var Q19;
            Q19=makeQuery(id+"F33.opExtrude","SWEPT_EDGE",EDGE,{"disambiguationData":[OSD([sQuery(id+"F0.wireOp",EDGE,"E1.0"),sQuery(id+"F32.wireOp",EDGE,"E33.left")])]});
            var Q20;
            Q20=makeQuery(id+"F33.opExtrude","SWEPT_EDGE",EDGE,{"disambiguationData":[OSD([sQuery(id+"F0.wireOp",EDGE,"E1.0"),sQuery(id+"F32.wireOp",EDGE,"E35.left")])]});
            var Q21;
            Q21=makeQuery(id+"F33.opExtrude","SWEPT_EDGE",EDGE,{"disambiguationData":[OSD([sQuery(id+"F0.wireOp",EDGE,"E1.0"),sQuery(id+"F32.wireOp",EDGE,"E35.right"),sQuery(id+"F32.wireOp",EDGE,"E38.trimOffspring")])]});
            var Q22;
            Q22=makeQuery(id+"F33.opExtrude","SWEPT_EDGE",EDGE,{"disambiguationData":[OSD([sQuery(id+"F0.wireOp",EDGE,"E1.2"),sQuery(id+"F32.wireOp",EDGE,"E30.right"),sQuery(id+"F32.wireOp",EDGE,"E40.trimOffspring")])]});
            var Q23;
            Q23=makeQuery(id+"F33.opExtrude","SWEPT_EDGE",EDGE,{"disambiguationData":[OSD([sQuery(id+"F0.wireOp",EDGE,"E1.2"),sQuery(id+"F32.wireOp",EDGE,"E30.bottom"),sQuery(id+"F32.wireOp",EDGE,"E30.left")])]});
            fillet(context, id + "F34", {"entities" : qUnion([Q0, Q1, Q2, Q3, Q4, Q5, Q6, Q7, Q8, Q9, Q10, Q11, Q12, Q13, Q14, Q15, Q16, Q17, Q18, Q19, Q20, Q21, Q22, Q23]), "radius" : 5 * mm, "tangentPropagation" : true, "allowEdgeOverflow" : false});
        }
        {
            var Q0;
            Q0=makeQuery(id+"F28.boolean.opBoolean","COPY",EDGE,{"derivedFrom":makeQuery(id+"F28.opSweep","CAP_EDGE",EDGE,{"disambiguationData":[OSD([sQuery(id+"F24.wireOp",VERTEX,"E26.end"),sQuery(id+"F27.wireOp",EDGE,"E27.bottom")])],"isStart":false})});
            fillet(context, id + "F35", {"entities" : qUnion([Q0]), "radius" : 5 * mm, "tangentPropagation" : true, "allowEdgeOverflow" : false});
        }
        {
            var Q0;
            Q0=makeQuery(id+"F35.opFillet","BLEND_EDGE",EDGE,{"blendedFrom":[makeQuery(id+"F28.boolean.opBoolean","COPY",EDGE,{"derivedFrom":makeQuery(id+"F28.opSweep","CAP_EDGE",EDGE,{"disambiguationData":[OSD([sQuery(id+"F24.wireOp",VERTEX,"E26.end"),sQuery(id+"F27.wireOp",EDGE,"E27.bottom")])],"isStart":false})}),makeQuery(id+"F12.opShell","OFFSET_FACE",FACE,{"disambiguationData":[OSD([sQuery(id+"F0.wireOp",EDGE,"E1.0"),sQuery(id+"F0.wireOp",EDGE,"E1.1"),sQuery(id+"F0.wireOp",EDGE,"E1.2"),sQuery(id+"F0.wireOp",EDGE,"E1.3"),sQuery(id+"F7.wireOp",EDGE,"E3.bottom")])]})],"blendedInto":[makeQuery(id+"F12.opShell","OFFSET_FACE",FACE,{"disambiguationData":[OSD([sQuery(id+"F0.wireOp",EDGE,"E1.0"),sQuery(id+"F0.wireOp",EDGE,"E1.1"),sQuery(id+"F0.wireOp",EDGE,"E1.2"),sQuery(id+"F0.wireOp",EDGE,"E1.3"),sQuery(id+"F7.wireOp",EDGE,"E3.bottom")])]})]});
            fillet(context, id + "F36", {"entities" : qUnion([Q0]), "radius" : 5 * mm, "tangentPropagation" : true, "allowEdgeOverflow" : false});
        }
    });
